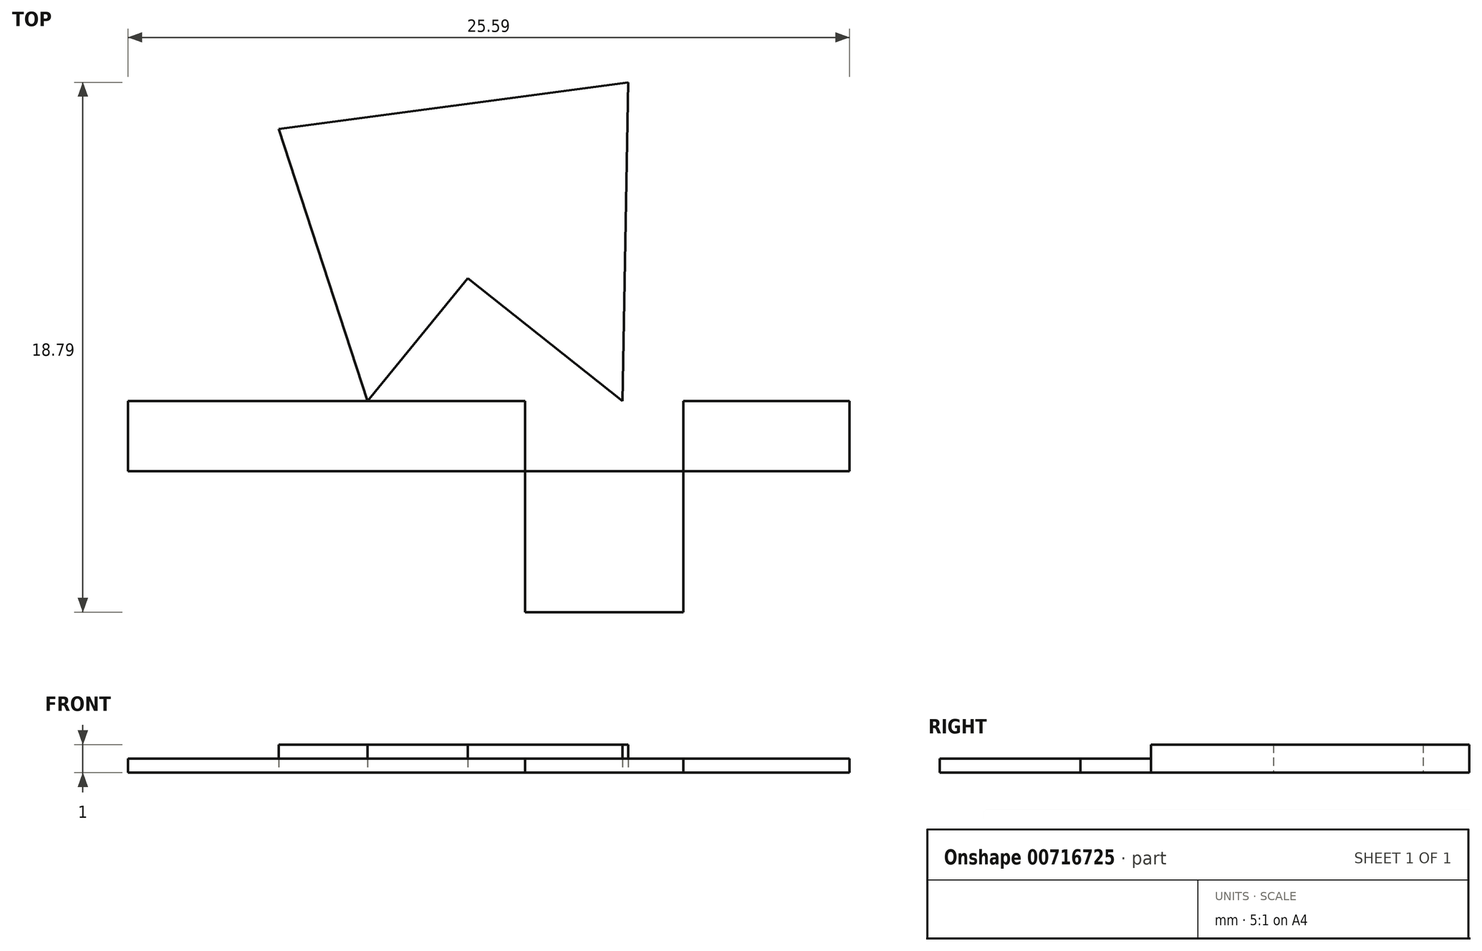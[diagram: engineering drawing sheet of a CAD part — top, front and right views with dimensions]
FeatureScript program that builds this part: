
annotation { "Feature Type Name" : "Feature", "Feature Type Description" : "" }
export const myFeature = defineFeature(function(context is Context, id is Id, definition is map)
    precondition{}
    {
        {
            var Q0;
            Q0=qCreatedBy(makeId("Top.planeOp"),FACE);
            var sketch = newSketch(context, id + "F0", { "sketchPlane" : qUnion([Q0])});
            skLineSegment(sketch, "E0", {"start": v(0, 0) * mm, "end": v(-9.05, 0) * mm});
            skLineSegment(sketch, "E1", {"start": v(-9.05, 0) * mm, "end": v(-12.2, 9.65) * mm});
            skLineSegment(sketch, "E2", {"start": v(-12.2, 9.65) * mm, "end": v(0, 0) * mm});
            skLineSegment(sketch, "E3", {"start": v(-9.05, 0) * mm, "end": v(0, 0) * mm});
            skLineSegment(sketch, "E4", {"start": v(0, 0) * mm, "end": v(0.2, 11.3) * mm});
            skLineSegment(sketch, "E5", {"start": v(0.2, 11.3) * mm, "end": v(-9.05, 0) * mm});
            skLineSegment(sketch, "E6", {"start": v(-12.2, 9.65) * mm, "end": v(0.2, 11.3) * mm});
            skSolve(sketch);
        }
        {
            var Q0;
            {var subQ0=sQuery(id+"F0.wireOp",EDGE,"E1");Q0=makeQuery(id+"F0.imprint","IMPRINT",FACE,{"disambiguationData":[TD([[makeQuery(id+"F0.imprint","IMPRINT",EDGE,{"derivedFrom":subQ0}),-1.0]])]});}
            var Q1;
            {var subQ0=sQuery(id+"F0.wireOp",EDGE,"E4");Q1=makeQuery(id+"F0.imprint","IMPRINT",FACE,{"disambiguationData":[TD([[makeQuery(id+"F0.imprint","IMPRINT",EDGE,{"derivedFrom":subQ0}),1.0]])]});}
            var Q2;
            {var subQ0=sQuery(id+"F0.wireOp",EDGE,"E6");Q2=makeQuery(id+"F0.imprint","IMPRINT",FACE,{"disambiguationData":[TD([[makeQuery(id+"F0.imprint","IMPRINT",EDGE,{"derivedFrom":subQ0}),-1.0]])]});}
            var Q3;
            {var subQ0=sQuery(id+"F0.wireOp",EDGE,"E3");Q3=makeQuery(id+"F0.imprint","IMPRINT",FACE,{"disambiguationData":[TD([[makeQuery(id+"F0.imprint","IMPRINT",EDGE,{"derivedFrom":subQ0}),1.0]])]});}
            extrude(context, id + "F1", {"entities" : qUnion([Q0, Q1, Q2, Q3]), "depth" : 1 * mm, "offsetDistance" : 25 * mm});
        }
        {
            var Q0;
            Q0=qCreatedBy(makeId("Top.planeOp"),FACE);
            var sketch = newSketch(context, id + "F2", { "sketchPlane" : qUnion([Q0])});
            skLineSegment(sketch, "E7.bottom", {"start": v(8.05, 0) * mm, "end": v(-17.54, 0) * mm});
            skLineSegment(sketch, "E7.top", {"start": v(8.05, -2.5) * mm, "end": v(-17.54, -2.5) * mm});
            skLineSegment(sketch, "E7.left", {"start": v(8.05, 0) * mm, "end": v(8.05, -2.5) * mm});
            skLineSegment(sketch, "E7.right", {"start": v(-17.54, 0) * mm, "end": v(-17.54, -2.5) * mm});
            skLineSegment(sketch, "E8.bottom", {"start": v(2.16, 0) * mm, "end": v(-3.45, 0) * mm});
            skLineSegment(sketch, "E8.top", {"start": v(2.16, -7.5) * mm, "end": v(-3.45, -7.5) * mm});
            skLineSegment(sketch, "E8.left", {"start": v(2.16, 0) * mm, "end": v(2.16, -7.5) * mm});
            skLineSegment(sketch, "E8.right", {"start": v(-3.45, 0) * mm, "end": v(-3.45, -7.5) * mm});
            skSolve(sketch);
        }
        {
            var Q0;
            {var subQ5=sQuery(id+"F2.wireOp",EDGE,"E8.bottom");Q0=makeQuery(id+"F2.imprint","IMPRINT",FACE,{"disambiguationData":[TD([[makeQuery(id+"F2.imprint","IMPRINT",EDGE,{"derivedFrom":subQ5}),1.0]])]});}
            var Q1;
            {var subQ0=sQuery(id+"F2.wireOp",EDGE,"E7.right");Q1=makeQuery(id+"F2.imprint","IMPRINT",FACE,{"disambiguationData":[TD([[makeQuery(id+"F2.imprint","IMPRINT",EDGE,{"derivedFrom":subQ0}),1.0]])]});}
            var Q2;
            {var subQ0=sQuery(id+"F2.wireOp",EDGE,"E7.left");Q2=makeQuery(id+"F2.imprint","IMPRINT",FACE,{"disambiguationData":[TD([[makeQuery(id+"F2.imprint","IMPRINT",EDGE,{"derivedFrom":subQ0}),-1.0]])]});}
            var Q3;
            {var subQ5=sQuery(id+"F2.wireOp",EDGE,"E8.top");Q3=makeQuery(id+"F2.imprint","IMPRINT",FACE,{"disambiguationData":[TD([[makeQuery(id+"F2.imprint","IMPRINT",EDGE,{"derivedFrom":subQ5}),-1.0]])]});}
            extrude(context, id + "F3", {"entities" : qUnion([Q0, Q1, Q2, Q3]), "operationType" : NewBodyOperationType.ADD, "depth" : 0.5 * mm, "offsetDistance" : 25 * mm});
        }
    });
